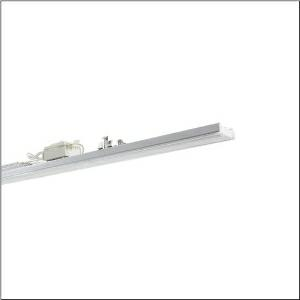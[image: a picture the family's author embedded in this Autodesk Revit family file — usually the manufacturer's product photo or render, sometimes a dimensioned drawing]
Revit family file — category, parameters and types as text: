
# Revit family: licross_r__11_recessed_ho_51tl12de47xm_0909
name_source: partatom
category: Lighting Fixtures
units: mm (PartAtom-declared; Revit-internal decimal feet)

## family parameters
Cut with Voids When Loaded = No
Host = Face
Light Source = No
Part Type = Normal
Room Calculation Point = No
Round Connector Dimension = Use Diameter
Shared = No

## types (1)
- --- (1 x LED, 7020 lm, 40.2 W, 4000K)
    Apparent Load = 40 VA
    CIE Flux Codes = 66 91 98 100 100
    Color Rendering = 80
    Color Temperature = 4000K
    Default Elevation = 1800 mm
    Description = Licross® 11 Recessed HO, luminaire insert, of sheet steel, coil coated, white, length: 750mm, width: 66mm, height: 67mm, LED rated luminous flux: 7.020lm, light colour: 840, control gear: DALI 2, with plug, 5-pole, with phase selection, mains connection: 220..240V, AC, 50/60Hz, rated input power: 40W, halogen-free wiring, primary optical cover: cover, of PMMA, light emission: direct distribution, primary light characteristic: symmetric, protection rating (complete): IP40, insulation class (complete): insulation class I (protective earthing), certification: CE, ENEC, VDE, UKCA, protection symbol: D if used in an environment without relevant dust loads with corresponding accessories, impact resistance: IK06, permissible ambient temperature for indoor applications: -25..+30°C, corresponds to IFS (International Featured Standards) requirements for safety and quality in the food industry, reducing of maximum allowable ambient temperature of 5°C with ceiling mounting, LABS conformity tested according to VDMA 24364:2018-05, packaging unit: 1 piece
    Height = 58 mm
    Lamp = 1 x LED
    Lamp Light Flux = 7020 lm
    Lamp Power = 40.2 W
    Lamp count = 1
    Length = 750 mm
    Luminous efficacy = 175 lm/W
    Manufacturer = Siteco
    ModVariant = No
    Model = 51TL12DE47XM
    Mounting Place = Ceiling
    Mounting Type = Pendant
    Number of Poles = 1
    OnlyDefault = Yes
    Power Factor = 1
    Product Name = Licross® 11 Recessed HO
    Product group = luminaire insert
    ProductGroupID = 902
    Protection Class = Protection class I
    Protection Degree = IP 40
    RLX_Detail_Level = 1
    RLX_Emergency_Light_Flux = 0 lm
    RLX_Emergency_Type = 0
    RLX_Emergency_Type_DB = No
    RlxData = <blob elided: 29097 chars, md5=c3573150>
    Socket = socket
    Standby Power = 0 W
    System Light Flux = 7020 lm
    System Power = 40 W
    Type Comments = factory setting: luminous flux: 100 % | dim-lin: 254 | 522 mA
    Type Image = l_1296930.jpg
    URL = http://relux.com
    VarID = @adj_099488
    Voltage = 0 V
    Weight = 0.00 kg
    Width = 66 mm

## geometry (parser evidence)
native form markers: Blend x4, Sweep x11
no freeform markers — native parametric forms only
